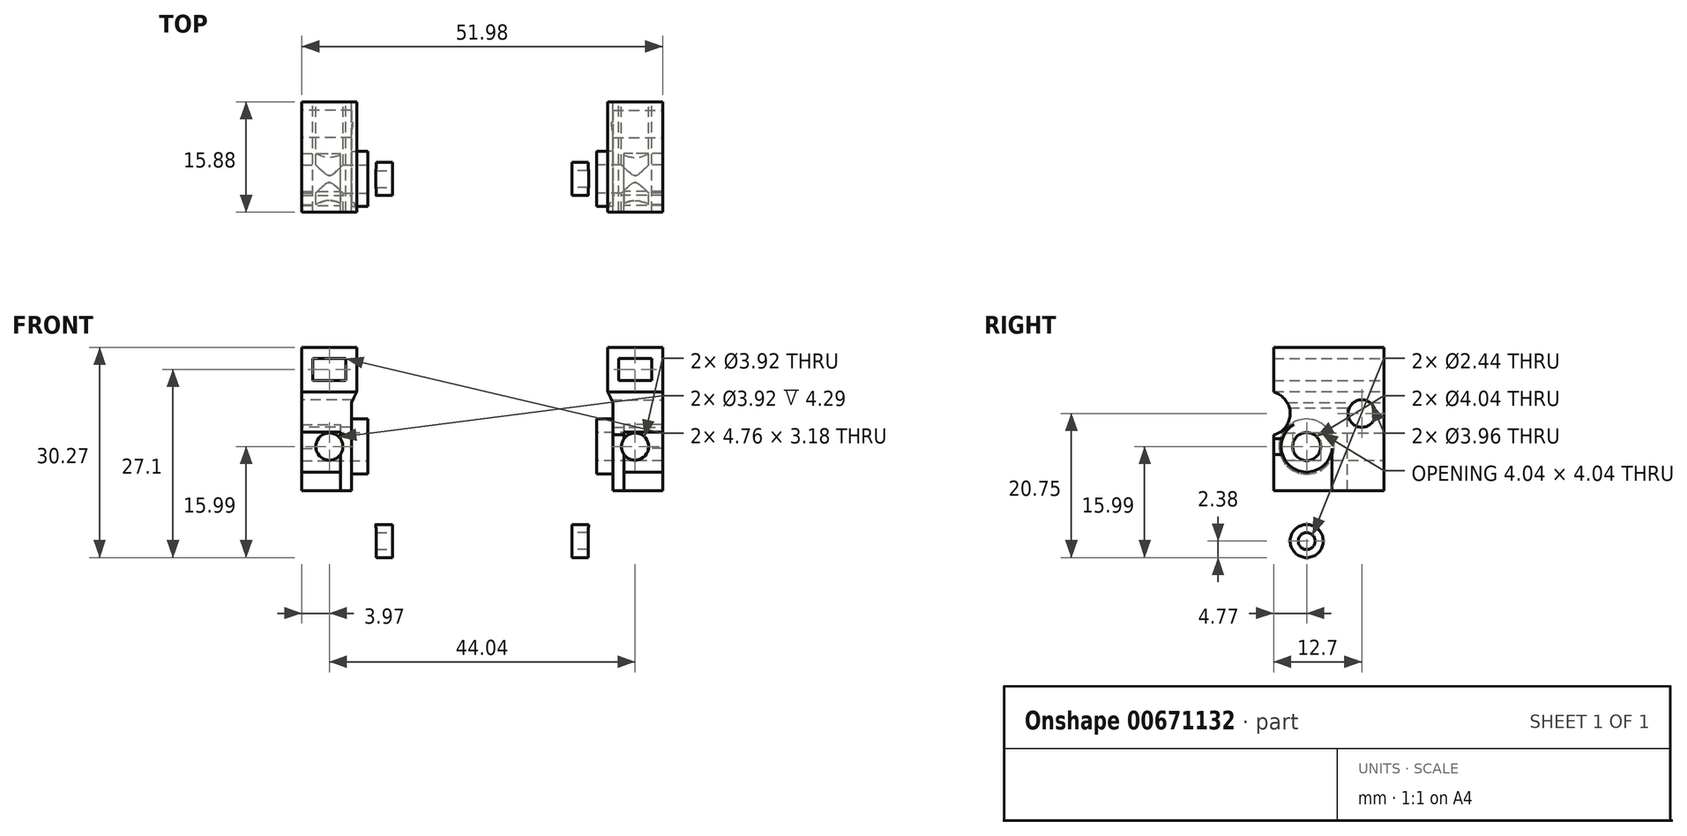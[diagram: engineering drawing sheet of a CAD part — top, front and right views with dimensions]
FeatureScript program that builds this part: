
annotation { "Feature Type Name" : "Feature", "Feature Type Description" : "" }
export const myFeature = defineFeature(function(context is Context, id is Id, definition is map)
    precondition{}
    {
        {
            var Q0;
            Q0=qCreatedBy(makeId("Front.planeOp"),FACE);
            var sketch = newSketch(context, id + "F0", { "sketchPlane" : qUnion([Q0])});
            skLineSegment(sketch, "E0", {"start": v(18.05, 32.8) * mm, "end": v(25.99, 32.8) * mm});
            skLineSegment(sketch, "E1", {"start": v(25.99, 32.8) * mm, "end": v(25.99, 23.28) * mm});
            skLineSegment(sketch, "E2", {"start": v(25.99, 23.28) * mm, "end": v(20.43, 23.28) * mm});
            skLineSegment(sketch, "E3", {"start": v(20.43, 23.28) * mm, "end": v(20.43, 12.17) * mm});
            skLineSegment(sketch, "E4", {"start": v(20.43, 12.17) * mm, "end": v(18.84, 12.17) * mm});
            skLineSegment(sketch, "E5", {"start": v(18.84, 12.17) * mm, "end": v(18.84, 24.87) * mm});
            skLineSegment(sketch, "E6", {"start": v(18.84, 24.87) * mm, "end": v(18.05, 26.46) * mm});
            skLineSegment(sketch, "E7", {"start": v(18.05, 32.8) * mm, "end": v(18.05, 26.46) * mm});
            skLineSegment(sketch, "E8.bottom", {"start": v(19.64, 31.22) * mm, "end": v(24.4, 31.22) * mm});
            skLineSegment(sketch, "E8.top", {"start": v(19.64, 28.04) * mm, "end": v(24.4, 28.04) * mm});
            skLineSegment(sketch, "E8.left", {"start": v(19.64, 31.22) * mm, "end": v(19.64, 28.04) * mm});
            skLineSegment(sketch, "E8.right", {"start": v(24.4, 31.22) * mm, "end": v(24.4, 28.04) * mm});
            skLineSegment(sketch, "E9", {"start": v(18.84, 23.28) * mm, "end": v(16.46, 23.28) * mm});
            skLineSegment(sketch, "E10", {"start": v(16.46, 23.28) * mm, "end": v(16.46, 6.73) * mm});
            skLineSegment(sketch, "E11", {"start": v(22.02, 32.8) * mm, "end": v(22.02, 5.2) * mm, "construction": true});
            skPoint(sketch, "E11.endSnap0", {"position": v(22.02, 28.04) * mm});
            skLineSegment(sketch, "E12", {"start": v(12.9, 12.67) * mm, "end": v(12.9, 2.53) * mm});
            skLineSegment(sketch, "E13", {"start": v(12.9, 2.53) * mm, "end": v(15.27, 2.53) * mm});
            skLineSegment(sketch, "E14", {"start": v(15.27, 2.53) * mm, "end": v(15.27, 9.81) * mm});
            skLineSegment(sketch, "E15", {"start": v(22.02, 5.2) * mm, "end": v(14.08, 5.2) * mm, "construction": true});
            skLineSegment(sketch, "E16", {"start": v(14.08, 5.2) * mm, "end": v(14.08, 20.14) * mm, "construction": true});
            skFitSpline(sketch, "E17", {"points": [v(15.27, 6.17) * mm, v(16.46, 9.18) * mm, v(18.84, 12.32) * mm], "startDerivative": vector(0, 8.88) * mm, "endDerivative": vector(0, 13.63) * mm});
            skFitSpline(sketch, "E18", {"points": [v(12.9, 7.06) * mm, v(14.37, 10.49) * mm, v(16.46, 13.4) * mm], "startDerivative": vector(0, 10.4) * mm, "endDerivative": vector(0, 13.7) * mm});
            skSolve(sketch);
        }
        {
            var Q0;
            Q0=qSketchRegion(id+"F0",true);
            extrude(context, id + "F1", {"entities" : qUnion([Q0]), "depth" : 15.88 * mm});
        }
        {
            var Q0;
            Q0=makeQuery(id+"F1.opExtrude","CAP_FACE",FACE,{"disambiguationData":[OSD([sQuery(id+"F0.wireOp",EDGE,"E0"),sQuery(id+"F0.wireOp",EDGE,"E1"),sQuery(id+"F0.wireOp",EDGE,"E2"),sQuery(id+"F0.wireOp",EDGE,"E3"),sQuery(id+"F0.wireOp",EDGE,"E4"),sQuery(id+"F0.wireOp",EDGE,"E5"),sQuery(id+"F0.wireOp",EDGE,"E6"),sQuery(id+"F0.wireOp",EDGE,"E7"),sQuery(id+"F0.wireOp",EDGE,"E8.bottom"),sQuery(id+"F0.wireOp",EDGE,"E8.top"),sQuery(id+"F0.wireOp",EDGE,"E8.left"),sQuery(id+"F0.wireOp",EDGE,"E8.right"),sQuery(id+"F0.wireOp",EDGE,"E9"),sQuery(id+"F0.wireOp",EDGE,"E10"),sQuery(id+"F0.wireOp",EDGE,"E12"),sQuery(id+"F0.wireOp",EDGE,"E13"),sQuery(id+"F0.wireOp",EDGE,"E14"),sQuery(id+"F0.wireOp",EDGE,"E17"),sQuery(id+"F0.wireOp",EDGE,"E18")])],"isStart":true});
            var sketch = newSketch(context, id + "F2", { "sketchPlane" : qUnion([Q0])});
            skLineSegment(sketch, "E19", {"start": v(-18.84, 23.28) * mm, "end": v(-18.84, 12.32) * mm});
            skSolve(sketch);
        }
        {
            var Q0;
            Q0=qSketchRegion(id+"F2",true);
            var Q1;
            Q1=makeQuery(id+"F2.imprint","IMPRINT",FACE,{"disambiguationData":[TD([[makeQuery(id+"F2.imprint","IMPRINT",EDGE,{"derivedFrom":sQuery(id+"F2.wireOp",EDGE,"E19")}),1.0]])]});
            extrude(context, id + "F3", {"entities" : qUnion([Q0, Q1]), "operationType" : NewBodyOperationType.REMOVE, "oppositeDirection" : true, "depth" : 6.35 * mm});
        }
        {
            var Q0;
            Q0=makeQuery(id+"F1.opExtrude","SWEPT_FACE",FACE,{"disambiguationData":[OSD([sQuery(id+"F0.wireOp",EDGE,"E10")])]});
            var sketch = newSketch(context, id + "F4", { "sketchPlane" : qUnion([Q0])});
            skCircle(sketch, "E20", {"center": v(11.11, 18.52) * mm, "radius": 2.02 * mm});
            skSolve(sketch);
        }
        {
            var Q0;
            Q0=qSketchRegion(id+"F4",true);
            extrude(context, id + "F5", {"entities" : qUnion([Q0]), "operationType" : NewBodyOperationType.REMOVE, "oppositeDirection" : true, "depth" : 6.35 * mm});
        }
        {
            var Q0;
            Q0=makeQuery(id+"F1.opExtrude","SWEPT_FACE",FACE,{"disambiguationData":[OSD([sQuery(id+"F0.wireOp",EDGE,"E12")])]});
            var sketch = newSketch(context, id + "F6", { "sketchPlane" : qUnion([Q0])});
            skCircle(sketch, "E21", {"center": v(11.11, 4.91) * mm, "radius": 1.22 * mm});
            skSolve(sketch);
        }
        {
            var Q0;
            Q0=qSketchRegion(id+"F6",true);
            extrude(context, id + "F7", {"entities" : qUnion([Q0]), "operationType" : NewBodyOperationType.REMOVE, "oppositeDirection" : true, "depth" : 3.17 * mm});
        }
        {
            var Q0;
            Q0=makeQuery(id+"F1.opExtrude","SWEPT_FACE",FACE,{"disambiguationData":[OSD([sQuery(id+"F0.wireOp",EDGE,"E12")])]});
            var sketch = newSketch(context, id + "F8", { "sketchPlane" : qUnion([Q0])});
            skCircle(sketch, "E22", {"center": v(11.11, 4.91) * mm, "radius": 2.38 * mm});
            skCircle(sketch, "E23", {"center": v(11.11, 18.52) * mm, "radius": 3.97 * mm});
            skLineSegment(sketch, "E24", {"start": v(7.17, 18.06) * mm, "end": v(8.75, 4.64) * mm});
            skLineSegment(sketch, "E25", {"start": v(15.05, 18.06) * mm, "end": v(13.48, 4.64) * mm});
            skLineSegment(sketch, "E26.bottom", {"start": v(5.27, 1.8) * mm, "end": v(17.26, 1.8) * mm});
            skLineSegment(sketch, "E26.top", {"start": v(5.27, 24.07) * mm, "end": v(17.26, 24.07) * mm});
            skLineSegment(sketch, "E26.left", {"start": v(5.27, 1.8) * mm, "end": v(5.27, 24.07) * mm});
            skLineSegment(sketch, "E26.right", {"start": v(17.26, 1.8) * mm, "end": v(17.26, 24.07) * mm});
            skSolve(sketch);
        }
        {
            var Q0;
            Q0=qSketchRegion(id+"F8",true);
            extrude(context, id + "F9", {"entities" : qUnion([Q0]), "operationType" : NewBodyOperationType.REMOVE, "oppositeDirection" : true, "depth" : 5.95 * mm});
        }
        {
            var Q0;
            {var subQ0=sQuery(id+"F0.wireOp",EDGE,"E5");Q0=makeQuery(id+"F9.boolean.opBoolean","MERGE",FACE,{"derivedFrom":[makeQuery(id+"F3.boolean.opBoolean","MERGE",FACE,{"derivedFrom":[makeQuery(id+"F1.opExtrude","SWEPT_FACE",FACE,{"disambiguationData":[OSD([subQ0]),TDD([makeQuery(id+"F0.imprint","IMPRINT",EDGE,{"disambiguationData":[TD([[makeQuery(id+"F0.imprint","INTERSECT",VERTEX,{"derivedFrom":[sQuery(id+"F0.wireOp",EDGE,"E4"),subQ0]}),-1.0]])],"derivedFrom":subQ0})])]}),makeQuery(id+"F1.opExtrude","SWEPT_FACE",FACE,{"disambiguationData":[OSD([subQ0]),TDD([makeQuery(id+"F0.imprint","IMPRINT",EDGE,{"disambiguationData":[TD([[makeQuery(id+"F0.imprint","INTERSECT",VERTEX,{"derivedFrom":[subQ0,sQuery(id+"F0.wireOp",EDGE,"E6")]}),1.0]])],"derivedFrom":subQ0})])]}),makeQuery(id+"F3.opExtrude","SWEPT_FACE",FACE,{"disambiguationData":[OSD([sQuery(id+"F2.wireOp",EDGE,"E19")])]})]}),makeQuery(id+"F9.opExtrude","CAP_FACE",FACE,{"disambiguationData":[OSD([sQuery(id+"F8.wireOp",EDGE,"E22"),sQuery(id+"F8.wireOp",EDGE,"E23"),sQuery(id+"F8.wireOp",EDGE,"E24"),sQuery(id+"F8.wireOp",EDGE,"E25"),sQuery(id+"F8.wireOp",EDGE,"E26.bottom"),sQuery(id+"F8.wireOp",EDGE,"E26.top"),sQuery(id+"F8.wireOp",EDGE,"E26.left"),sQuery(id+"F8.wireOp",EDGE,"E26.right")])],"isStart":false})]});}
            var sketch = newSketch(context, id + "F10", { "sketchPlane" : qUnion([Q0])});
            skCircle(sketch, "E27", {"center": v(3.18, 23.28) * mm, "radius": 1.98 * mm});
            skLineSegment(sketch, "E28", {"start": v(3.08, 25.26) * mm, "end": v(0, 25.26) * mm});
            skLineSegment(sketch, "E29", {"start": v(3.12, 21.3) * mm, "end": v(0, 21.3) * mm});
            skLineSegment(sketch, "E30", {"start": v(0, 25.26) * mm, "end": v(0, 21.3) * mm});
            skSolve(sketch);
        }
        {
            var Q0;
            Q0=qSketchRegion(id+"F10",true);
            extrude(context, id + "F11", {"entities" : qUnion([Q0]), "operationType" : NewBodyOperationType.REMOVE, "endBound" : BoundingType.SYMMETRIC, "depth" : 25.4 * mm});
        }
        {
            var Q0;
            Q0=makeQuery(id+"F1.opExtrude","SWEPT_FACE",FACE,{"disambiguationData":[OSD([sQuery(id+"F0.wireOp",EDGE,"E7")])]});
            var sketch = newSketch(context, id + "F12", { "sketchPlane" : qUnion([Q0])});
            skCircle(sketch, "E31", {"center": v(16.67, 23.28) * mm, "radius": 3.18 * mm});
            skSolve(sketch);
        }
        {
            var Q0;
            Q0=qSketchRegion(id+"F12",true);
            extrude(context, id + "F13", {"entities" : qUnion([Q0]), "operationType" : NewBodyOperationType.REMOVE, "oppositeDirection" : true, "depth" : 25.4 * mm});
        }
        {
            var Q0;
            Q0=qCreatedBy(makeId("Right.planeOp"),FACE);
            var sketch = newSketch(context, id + "F14", { "sketchPlane" : qUnion([Q0])});
            skLineSegment(sketch, "E32.bottom", {"start": v(-29.03, 45.11) * mm, "end": v(-6.29, 45.11) * mm});
            skLineSegment(sketch, "E32.top", {"start": v(-29.03, 24.7) * mm, "end": v(-6.29, 24.7) * mm});
            skLineSegment(sketch, "E32.left", {"start": v(-29.03, 45.11) * mm, "end": v(-29.03, 24.7) * mm});
            skLineSegment(sketch, "E32.right", {"start": v(-6.29, 45.11) * mm, "end": v(-6.29, 24.7) * mm});
            skSolve(sketch);
        }
        {
            var Q0;
            Q0=makeQuery(id+"F1.opExtrude","SWEPT_FACE",FACE,{"disambiguationData":[OSD([sQuery(id+"F0.wireOp",EDGE,"E3")])]});
            var sketch = newSketch(context, id + "F15", { "sketchPlane" : qUnion([Q0])});
            skCircle(sketch, "E33", {"center": v(-11.11, 18.52) * mm, "radius": 3.67 * mm});
            skLineSegment(sketch, "E34", {"start": v(-15.15, 20.5) * mm, "end": v(-12.87, 21.74) * mm});
            skLineSegment(sketch, "E35", {"start": v(-7.45, 18.66) * mm, "end": v(-7.45, 12.17) * mm});
            skSolve(sketch);
        }
        {
            var Q0;
            {var subQ0=sQuery(id+"F15.wireOp",EDGE,"E35");var subQ1=sQuery(id+"F15.wireOp",EDGE,"E33");var subQ2=makeQuery(id+"F15.imprint","INTERSECT",VERTEX,{"disambiguationData":[OD(0.0)],"derivedFrom":[subQ1,subQ0]});Q0=makeQuery(id+"F15.imprint","IMPRINT",FACE,{"disambiguationData":[TD([[makeQuery(id+"F15.imprint","IMPRINT",EDGE,{"disambiguationData":[TD([[subQ2,1.0]])],"derivedFrom":subQ1}),1.0]])]});}
            var Q1;
            {var subQ6=sQuery(id+"F15.wireOp",EDGE,"E34");Q1=makeQuery(id+"F15.imprint","IMPRINT",FACE,{"disambiguationData":[TD([[makeQuery(id+"F15.imprint","IMPRINT",EDGE,{"derivedFrom":subQ6}),1.0]])]});}
            extrude(context, id + "F16", {"entities" : qUnion([Q0, Q1]), "operationType" : NewBodyOperationType.ADD, "depth" : 5.56 * mm});
        }
        {
            var Q0;
            {var subQ0=sQuery(id+"F0.wireOp",EDGE,"E3");var subQ1=sQuery(id+"F0.wireOp",EDGE,"E6");var subQ2=sQuery(id+"F0.wireOp",EDGE,"E5");var subQ3=sQuery(id+"F0.wireOp",EDGE,"E9");var subQ4=sQuery(id+"F0.wireOp",EDGE,"E4");var subQ5=sQuery(id+"F0.wireOp",EDGE,"E17");Q0=makeQuery(id+"F16.boolean.opBoolean","MERGE",FACE,{"derivedFrom":[makeQuery(id+"F11.boolean.opBoolean","SPLIT",FACE,{"disambiguationData":[TD([makeQuery(id+"F1.opExtrude","SWEPT_FACE",FACE,{"disambiguationData":[OSD([subQ0])]})])],"derivedFrom":makeQuery(id+"F1.opExtrude","CAP_FACE",FACE,{"disambiguationData":[OSD([sQuery(id+"F0.wireOp",EDGE,"E0"),sQuery(id+"F0.wireOp",EDGE,"E1"),sQuery(id+"F0.wireOp",EDGE,"E2"),subQ0,subQ4,subQ2,subQ1,sQuery(id+"F0.wireOp",EDGE,"E7"),sQuery(id+"F0.wireOp",EDGE,"E8.bottom"),sQuery(id+"F0.wireOp",EDGE,"E8.top"),sQuery(id+"F0.wireOp",EDGE,"E8.left"),sQuery(id+"F0.wireOp",EDGE,"E8.right"),subQ3,sQuery(id+"F0.wireOp",EDGE,"E10"),sQuery(id+"F0.wireOp",EDGE,"E12"),sQuery(id+"F0.wireOp",EDGE,"E13"),sQuery(id+"F0.wireOp",EDGE,"E14"),subQ5,sQuery(id+"F0.wireOp",EDGE,"E18")])],"isStart":true})}),makeQuery(id+"F16.opExtrude","SWEPT_FACE",FACE,{"disambiguationData":[OSD([subQ0])]})]});}
            var sketch = newSketch(context, id + "F17", { "sketchPlane" : qUnion([Q0])});
            skCircle(sketch, "E36", {"center": v(-22.02, 18.52) * mm, "radius": 1.96 * mm});
            skSolve(sketch);
        }
        {
            var Q0;
            Q0=qSketchRegion(id+"F17",true);
            extrude(context, id + "F18", {"entities" : qUnion([Q0]), "operationType" : NewBodyOperationType.REMOVE, "oppositeDirection" : true, "depth" : 25.4 * mm});
        }
        {
            var Q0;
            Q0=makeQuery(id+"F1.opExtrude","SWEPT_BODY",BODY,{"disambiguationData":[OSD([sQuery(id+"F0.wireOp",EDGE,"E0"),sQuery(id+"F0.wireOp",EDGE,"E1"),sQuery(id+"F0.wireOp",EDGE,"E2"),sQuery(id+"F0.wireOp",EDGE,"E3"),sQuery(id+"F0.wireOp",EDGE,"E4"),sQuery(id+"F0.wireOp",EDGE,"E5"),sQuery(id+"F0.wireOp",EDGE,"E6"),sQuery(id+"F0.wireOp",EDGE,"E7"),sQuery(id+"F0.wireOp",EDGE,"E8.bottom"),sQuery(id+"F0.wireOp",EDGE,"E8.top"),sQuery(id+"F0.wireOp",EDGE,"E8.left"),sQuery(id+"F0.wireOp",EDGE,"E8.right"),sQuery(id+"F0.wireOp",EDGE,"E9"),sQuery(id+"F0.wireOp",EDGE,"E10"),sQuery(id+"F0.wireOp",EDGE,"E12"),sQuery(id+"F0.wireOp",EDGE,"E13"),sQuery(id+"F0.wireOp",EDGE,"E14"),sQuery(id+"F0.wireOp",EDGE,"E17"),sQuery(id+"F0.wireOp",EDGE,"E18")])]});
            var Q1;
            Q1=makeQuery(id+"F14.imprint","IMPRINT",FACE,{"disambiguationData":[TD([[makeQuery(id+"F14.imprint","IMPRINT",EDGE,{"derivedFrom":sQuery(id+"F14.wireOp",EDGE,"E32.bottom")}),-1.0]])]});
            mirror(context, id + "F19", {"entities" : qUnion([Q0]), "mirrorPlane" : qUnion([Q1])});
        }
    });
